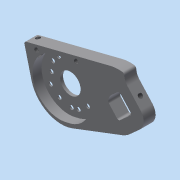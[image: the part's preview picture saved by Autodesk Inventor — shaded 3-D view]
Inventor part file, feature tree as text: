
AUTODESK INVENTOR PART (.ipt)
format: ipt  version: 2014 SP1 (Build 180222100, 222)  size: 406,016 bytes
history: native  units: in
note: dims shown in document units (in); Inventor stores cm internally (conversion verified against a paired STEP export)
features: sketch x9, extrude x7, thread x6, projected_geometry x4, fillet x3, other x1, chamfer x1
ambient origin geometry x8: Origin, YZ Plane, XZ Plane, XY Plane, X Axis, Y Axis, Z Axis, Center Point
bodies: Solid3 (feature_tree)
feature tree (31):
  other  "mountsketch_alt.ipt"
  extrude  "Extrusion11"  TaperAngle=360.0deg  [1 undecoded]
  fillet  "Fillet7"  Radius=0.5in
  sketch  "Sketch17"  dims[d94=0.1in d95=0.5in d99=0.19in d100=0.19in d101=0.355in]
  sketch  "Sketch12"  dims[d0=0.3937in]
  extrude  "Extrusion13"  Depth=1.0in
  extrude  "Extrusion14"  Depth=0.19in
  thread  "Thread5"  [1 undecoded]
  thread  "Thread6"  [1 undecoded]
  sketch  "Sketch16"  dims[d92=0.0in d93=1.0in]
  extrude  "Extrusion15"  Depth=1.0in TaperAngle=0.0deg
  fillet  "Fillet8"  Radius=1.0in
  fillet  "Fillet9"  Radius=1.0in
  sketch  "Sketch18"  dims[d102=0.25in d105=1.0in d106=0.0in d107=1.0in d108=0.0in d109=1.0in d110=0.0in]
  sketch  "Sketch19"  dims[d111=1.0in d112=0.0in d117=3.9751in d118=2.5984in]
  extrude  "Extrusion17"  Depth=3.9751in
  thread  "Thread7"  [1 undecoded]
  extrude  "Extrusion18"  TaperAngle=0.0deg  [1 undecoded]
  chamfer  "Chamfer1"  Distance=0.0938in
  thread  "Thread12"  [1 undecoded]
  thread  "Thread13"  [1 undecoded]
  extrude  "Extrusion21"  Depth=0.1in
  thread  "Thread14"  [1 undecoded]
  projected_geometry  "Projected Loop3"
  sketch  "Sketch13"  dims[d2=0.8661in d3=0.1693in d5=0.8661in d6=2.5984in d7=2.4577in d13=1.5748in d17=2.454in d18=1.9042in d15=360.0deg d91=0.5in]
  projected_geometry  "Projected Loop4"
  projected_geometry  "Projected Loop5"
  sketch  "Sketch21"  dims[d120=0.375in d121=0.0in]
  sketch  "Sketch22"  dims[d122=0.25in]
  sketch  "Sketch26"  dims[d123=0.2in d124=0.0938in d125=2.5984in d126=4.7534in d127=0.1in d128=2.5984in d129=4.7983in d136=0.5in d137=0.0in d138=0.19in d140=0.15in d142=1.0in d143=0.0in d146=2.5063in d147=0.9398in d148=2.2047in d149=0.19in d150=0.19in d153=0.5in d154=0.0in d161=0.0866in d162=0.125in d163=45.0deg d167=0.25in d178=2.2835in d179=2.2835in d181=0.5in d182=0.1875in d184=0.1875in d185=1.72in d188=1.0in d189=0.0in d190=1.0in d191=0.0in d192=0.19in d193=0.15in d194=0.15in d195=1.0in d196=0.0in d197=1.0in d198=0.0in]
  projected_geometry  "Projected Loop6"
note: 8 required parameter values undecoded (feature->parameter linkage not recoverable at this tier; creation-order binding heuristic only, values carry confidence <= 0.55)
